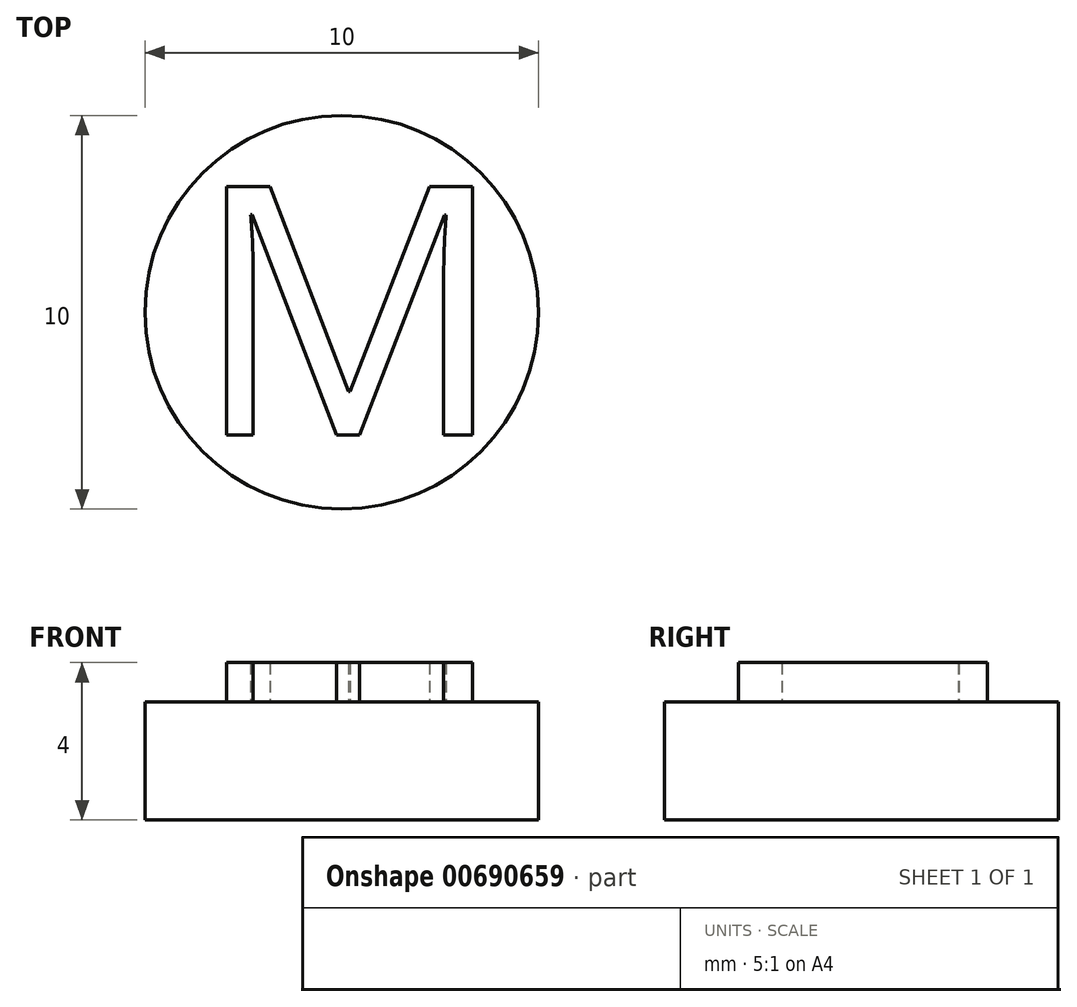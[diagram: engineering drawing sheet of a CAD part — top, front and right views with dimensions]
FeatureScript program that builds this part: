
annotation { "Feature Type Name" : "Feature", "Feature Type Description" : "" }
export const myFeature = defineFeature(function(context is Context, id is Id, definition is map)
    precondition{}
    {
        {
            var Q0;
            Q0=qCreatedBy(makeId("Top.planeOp"),FACE);
            var sketch = newSketch(context, id + "F0", { "sketchPlane" : qUnion([Q0])});
            skCircle(sketch, "E0", {"center": v(0, 0) * mm, "radius": 5 * mm});
            skSolve(sketch);
        }
        {
            var Q0;
            Q0 = qSketchRegion(id + "F0", true);
            extrude(context, id + "F1", {"entities" : qUnion([Q0]), "depth" : 3 * mm, "offsetDistance" : 25 * mm});
        }
        {
            var Q0;
            Q0=makeQuery(id+"F1.opExtrude","CAP_FACE",FACE,{"disambiguationData":[OSD([sQuery(id+"F0.wireOp",EDGE,"E0")])],"isStart":false});
            var sketch = newSketch(context, id + "F2", { "sketchPlane" : qUnion([Q0])});
            skText(sketch, "E1", { "text": "M", "fontName": "OpenSans-Regular.ttf"});
            const initialGuessF2  = {"E1": [-0.0038, -0.00312, 1, 0, 0.00637]};
            skSetInitialGuess(sketch, initialGuessF2);
            skSolve(sketch);
        }
        {
            var Q0;
            Q0 = qSketchRegion(id + "F2", true);
            extrude(context, id + "F3", {"entities" : qUnion([Q0]), "operationType" : NewBodyOperationType.ADD, "depth" : 1 * mm, "offsetDistance" : 25 * mm});
        }
    });
